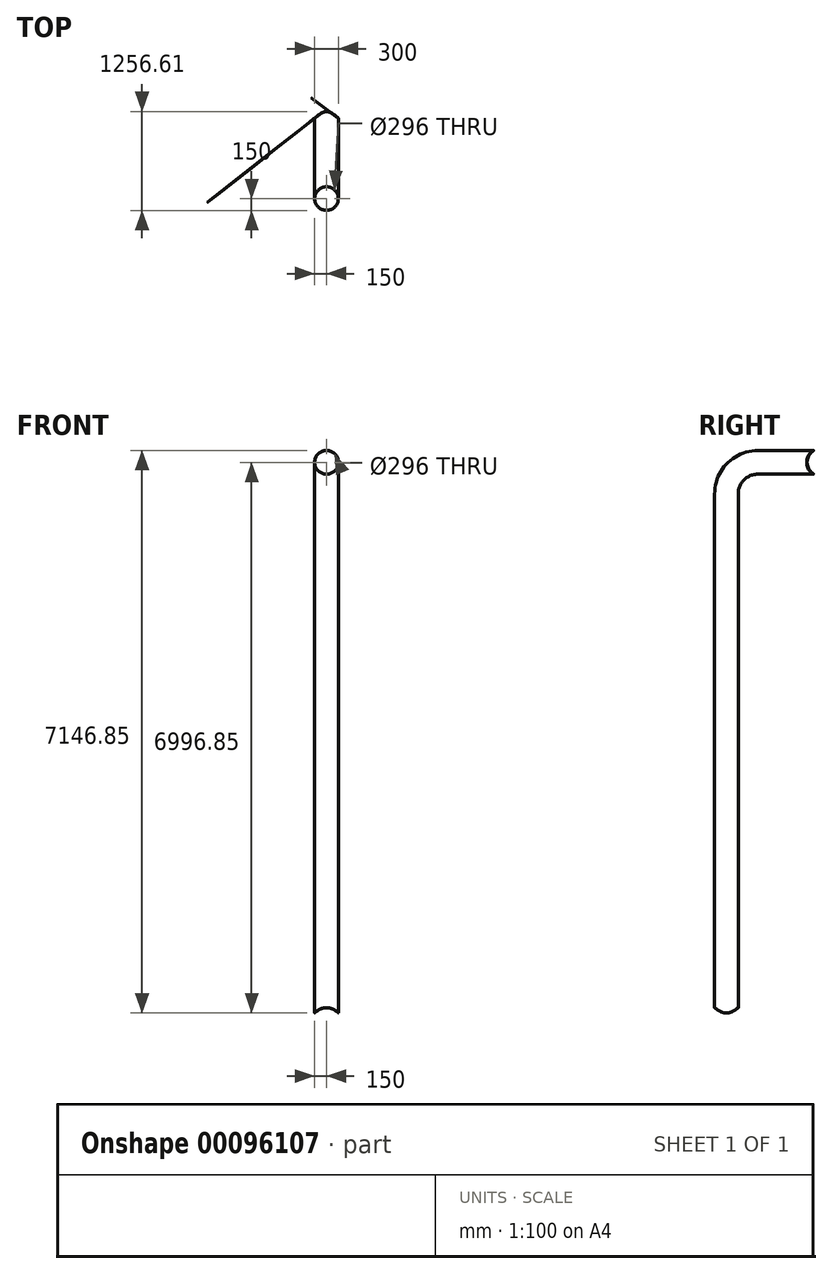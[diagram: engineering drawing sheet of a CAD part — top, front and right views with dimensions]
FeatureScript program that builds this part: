
annotation { "Feature Type Name" : "Feature", "Feature Type Description" : "" }
export const myFeature = defineFeature(function(context is Context, id is Id, definition is map)
    precondition{}
    {
        {
            var Q0;
            Q0=qCreatedBy(makeId("Front.planeOp"),FACE);
            var sketch = newSketch(context, id + "F0", { "sketchPlane" : qUnion([Q0])});
            skCircle(sketch, "E0", {"center": v(0, 0) * mm, "radius": 150 * mm});
            skCircle(sketch, "E1", {"center": v(0, 0) * mm, "radius": 148 * mm});
            skSolve(sketch);
        }
        {
            var Q0;
            Q0=qCreatedBy(makeId("Right.planeOp"),FACE);
            var sketch = newSketch(context, id + "F1", { "sketchPlane" : qUnion([Q0])});
            skLineSegment(sketch, "E2", {"start": v(0, 0) * mm, "end": v(-800, 0) * mm});
            skLineSegment(sketch, "E3", {"start": v(-1200, -400) * mm, "end": v(-1200, -7000) * mm});
            skPoint(sketch, "E4.visualSharp", {"position": v(-1200, 0) * mm});
            skArc(sketch, "E4.filletArc", {"start": v(-800, 0) * mm, "mid": v(-1082.84, -117.16) * mm, "end": v(-1200, -400) * mm});
            skPoint(sketch, "E5", {"position": v(0, 0) * mm});
            skCircle(sketch, "E6", {"center": v(0, 0) * mm, "radius": 175 * mm});
            skSolve(sketch);
        }
        {
            var Q0;
            Q0=makeQuery(id+"F0.imprint","IMPRINT",FACE,{"disambiguationData":[TD([[makeQuery(id+"F0.imprint","IMPRINT",EDGE,{"derivedFrom":sQuery(id+"F0.wireOp",EDGE,"E0")}),1.0]])]});
            var Q1;
            Q1=sQuery(id+"F1.wireOp",EDGE,"E2");
            var Q2;
            Q2=sQuery(id+"F1.wireOp",EDGE,"E4.filletArc");
            var Q3;
            Q3=sQuery(id+"F1.wireOp",EDGE,"E3");
            sweep(context, id + "F2", {"profiles" : qUnion([Q0]), "path" : qUnion([Q1, Q2, Q3])});
        }
        {
            var Q0;
            Q0=makeQuery(id+"F1.imprint","IMPRINT",FACE,{"disambiguationData":[TD([[makeQuery(id+"F1.imprint","IMPRINT",EDGE,{"derivedFrom":sQuery(id+"F1.wireOp",EDGE,"E6")}),1.0]])]});
            extrude(context, id + "F3", {"entities" : qUnion([Q0]), "operationType" : NewBodyOperationType.REMOVE, "endBound" : BoundingType.SYMMETRIC, "depth" : 300 * mm});
        }
        {
            var Q0;
            Q0=makeQuery(id+"F3.boolean.opBoolean","INTERSECT",EDGE,{"disambiguationData":[OD(0.0)],"derivedFrom":[makeQuery(id+"F2.opSweep","SWEPT_FACE",FACE,{"disambiguationData":[OSD([sQuery(id+"F0.wireOp",EDGE,"E0"),sQuery(id+"F1.wireOp",EDGE,"E2")])]}),makeQuery(id+"F3.opExtrude","SWEPT_FACE",FACE,{"disambiguationData":[OSD([sQuery(id+"F1.wireOp",EDGE,"E6")])]})]});
            var Q1;
            Q1=makeQuery(id+"F3.boolean.opBoolean","INTERSECT",EDGE,{"disambiguationData":[OD(1.0)],"derivedFrom":[makeQuery(id+"F2.opSweep","SWEPT_FACE",FACE,{"disambiguationData":[OSD([sQuery(id+"F0.wireOp",EDGE,"E0"),sQuery(id+"F1.wireOp",EDGE,"E2")])]}),makeQuery(id+"F3.opExtrude","SWEPT_FACE",FACE,{"disambiguationData":[OSD([sQuery(id+"F1.wireOp",EDGE,"E6")])]})]});
            fillet(context, id + "F4", {"entities" : qUnion([Q0, Q1]), "radius" : 5 * mm, "tangentPropagation" : true, "allowEdgeOverflow" : false});
        }
        {
            var Q0;
            Q0=qCreatedBy(makeId("Front.planeOp"),FACE);
            var sketch = newSketch(context, id + "F5", { "sketchPlane" : qUnion([Q0])});
            skCircle(sketch, "E7", {"center": v(0, -7129.13) * mm, "radius": 200 * mm});
            skSolve(sketch);
        }
        {
            var Q0;
            Q0=makeQuery(id+"F5.imprint","IMPRINT",FACE,{"disambiguationData":[TD([[makeQuery(id+"F5.imprint","IMPRINT",EDGE,{"derivedFrom":sQuery(id+"F5.wireOp",EDGE,"E7")}),1.0]])]});
            extrude(context, id + "F6", {"entities" : qUnion([Q0]), "operationType" : NewBodyOperationType.REMOVE, "endBound" : BoundingType.THROUGH_ALL, "depth" : 25 * mm});
        }
    });
